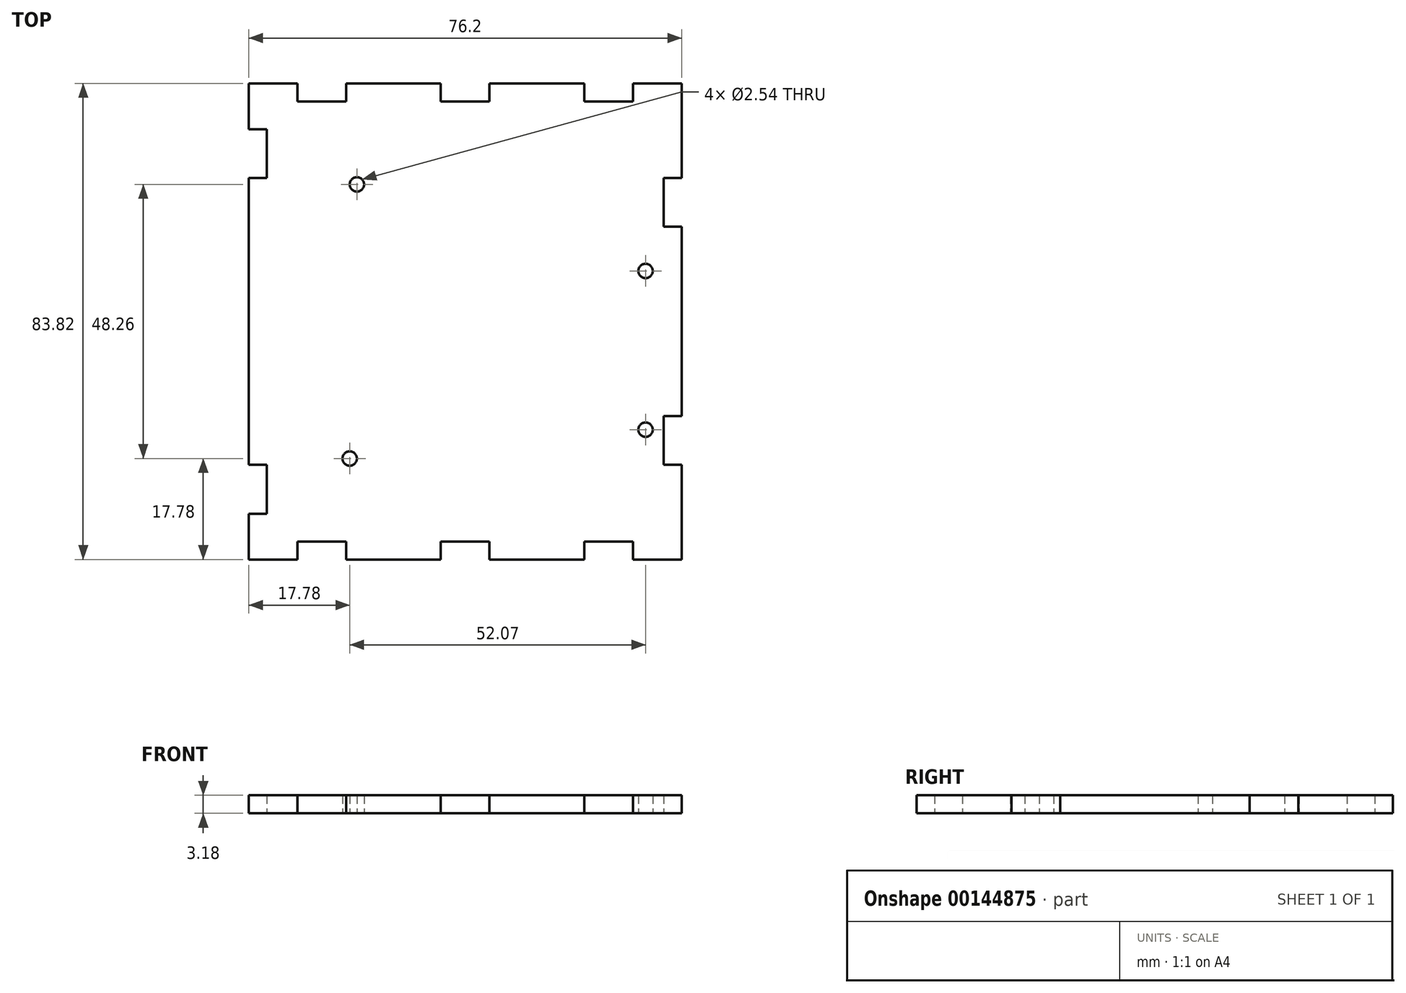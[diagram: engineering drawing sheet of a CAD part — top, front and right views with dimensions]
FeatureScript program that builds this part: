
annotation { "Feature Type Name" : "Feature", "Feature Type Description" : "" }
export const myFeature = defineFeature(function(context is Context, id is Id, definition is map)
    precondition{}
    {
        {
            var Q0;
            Q0=qCreatedBy(makeId("Top.planeOp"),FACE);
            var sketch = newSketch(context, id + "F0", { "sketchPlane" : qUnion([Q0])});
            skLineSegment(sketch, "E0.bottom", {"start": v(-38.1, 41.91) * mm, "end": v(38.1, 41.91) * mm});
            skLineSegment(sketch, "E0.top", {"start": v(-38.1, -41.91) * mm, "end": v(38.1, -41.91) * mm});
            skLineSegment(sketch, "E0.left", {"start": v(-38.1, 41.91) * mm, "end": v(-38.1, -41.9) * mm});
            skLineSegment(sketch, "E0.right", {"start": v(38.1, 41.91) * mm, "end": v(38.1, -41.9) * mm});
            skPoint(sketch, "E0.middle", {"position": v(0, 0) * mm});
            skCircle(sketch, "E1", {"center": v(-19.05, 24.13) * mm, "radius": 1.27 * mm});
            skCircle(sketch, "E2", {"center": v(-20.32, -24.13) * mm, "radius": 1.27 * mm});
            skCircle(sketch, "E3", {"center": v(31.75, 8.9) * mm, "radius": 1.27 * mm});
            skCircle(sketch, "E4", {"center": v(31.75, -19.05) * mm, "radius": 1.27 * mm});
            skPoint(sketch, "E5", {"position": v(-29.53, 41.91) * mm});
            skPoint(sketch, "E6", {"position": v(-20.95, 41.9) * mm});
            skPoint(sketch, "E7", {"position": v(0, 41.9) * mm});
            skPoint(sketch, "E8", {"position": v(0, 41.91) * mm});
            skPoint(sketch, "E9", {"position": v(20.94, 41.91) * mm});
            skPoint(sketch, "E10", {"position": v(29.51, 41.91) * mm});
            skLineSegment(sketch, "E11", {"start": v(-29.53, 41.91) * mm, "end": v(-29.53, 38.74) * mm});
            skLineSegment(sketch, "E12", {"start": v(-29.53, 38.74) * mm, "end": v(-20.95, 38.74) * mm});
            skLineSegment(sketch, "E13", {"start": v(-20.95, 38.74) * mm, "end": v(-20.95, 41.9) * mm});
            skLineSegment(sketch, "E14", {"start": v(0, 38.74) * mm, "end": v(0, 41.9) * mm});
            skLineSegment(sketch, "E15", {"start": v(20.94, 41.91) * mm, "end": v(20.94, 38.74) * mm});
            skLineSegment(sketch, "E16", {"start": v(20.94, 38.74) * mm, "end": v(29.51, 38.74) * mm});
            skLineSegment(sketch, "E17", {"start": v(29.51, 38.74) * mm, "end": v(29.51, 41.91) * mm});
            skLineSegment(sketch, "E18", {"start": v(0, 41.91) * mm, "end": v(-4.3, 41.91) * mm});
            skPoint(sketch, "E19", {"position": v(4.3, 41.91) * mm});
            skLineSegment(sketch, "E20", {"start": v(0, 41.91) * mm, "end": v(4.3, 41.91) * mm});
            skLineSegment(sketch, "E21", {"start": v(4.3, 41.91) * mm, "end": v(4.3, 38.74) * mm});
            skLineSegment(sketch, "E22", {"start": v(4.3, 38.74) * mm, "end": v(-4.3, 38.74) * mm});
            skLineSegment(sketch, "E23", {"start": v(-4.3, 38.74) * mm, "end": v(-4.3, 41.91) * mm});
            skPoint(sketch, "E24", {"position": v(-29.53, -41.9) * mm});
            skPoint(sketch, "E25", {"position": v(-20.95, -41.9) * mm});
            skPoint(sketch, "E26", {"position": v(-4.3, -41.91) * mm});
            skPoint(sketch, "E27", {"position": v(4.3, -41.91) * mm});
            skPoint(sketch, "E28", {"position": v(20.94, -41.91) * mm});
            skPoint(sketch, "E29", {"position": v(29.51, -41.91) * mm});
            skLineSegment(sketch, "E30.bottom", {"start": v(-29.53, -41.91) * mm, "end": v(-20.95, -41.91) * mm});
            skLineSegment(sketch, "E30.top", {"start": v(-29.53, -38.74) * mm, "end": v(-20.95, -38.74) * mm});
            skLineSegment(sketch, "E30.left", {"start": v(-29.53, -41.9) * mm, "end": v(-29.53, -38.74) * mm});
            skLineSegment(sketch, "E30.right", {"start": v(-20.95, -41.9) * mm, "end": v(-20.95, -38.74) * mm});
            skLineSegment(sketch, "E31.bottom", {"start": v(-4.3, -41.91) * mm, "end": v(4.3, -41.91) * mm});
            skLineSegment(sketch, "E31.top", {"start": v(-4.3, -38.74) * mm, "end": v(4.3, -38.74) * mm});
            skLineSegment(sketch, "E31.left", {"start": v(-4.3, -41.91) * mm, "end": v(-4.3, -38.74) * mm});
            skLineSegment(sketch, "E31.right", {"start": v(4.3, -41.91) * mm, "end": v(4.3, -38.74) * mm});
            skLineSegment(sketch, "E32.bottom", {"start": v(20.94, -41.91) * mm, "end": v(29.51, -41.91) * mm});
            skLineSegment(sketch, "E32.top", {"start": v(20.94, -38.74) * mm, "end": v(29.51, -38.74) * mm});
            skLineSegment(sketch, "E32.left", {"start": v(20.94, -41.91) * mm, "end": v(20.94, -38.74) * mm});
            skLineSegment(sketch, "E32.right", {"start": v(29.51, -41.91) * mm, "end": v(29.51, -38.74) * mm});
            skPoint(sketch, "E33", {"position": v(38.1, 20.96) * mm});
            skPoint(sketch, "E34", {"position": v(38.1, -20.96) * mm});
            skPoint(sketch, "E35", {"position": v(38.1, 0) * mm});
            skPoint(sketch, "E36", {"position": v(38.1, 25.25) * mm});
            skPoint(sketch, "E37", {"position": v(38.1, 16.66) * mm});
            skPoint(sketch, "E38", {"position": v(38.1, -16.66) * mm});
            skPoint(sketch, "E39", {"position": v(38.1, -25.25) * mm});
            skLineSegment(sketch, "E40.bottom", {"start": v(38.1, 25.25) * mm, "end": v(34.93, 25.25) * mm});
            skLineSegment(sketch, "E40.top", {"start": v(38.1, 16.66) * mm, "end": v(34.93, 16.66) * mm});
            skLineSegment(sketch, "E40.left", {"start": v(38.1, 25.25) * mm, "end": v(38.1, 16.66) * mm});
            skLineSegment(sketch, "E40.right", {"start": v(34.93, 25.25) * mm, "end": v(34.93, 16.66) * mm});
            skLineSegment(sketch, "E41.bottom", {"start": v(38.1, -16.66) * mm, "end": v(34.93, -16.66) * mm});
            skLineSegment(sketch, "E41.top", {"start": v(38.1, -25.25) * mm, "end": v(34.93, -25.25) * mm});
            skLineSegment(sketch, "E41.left", {"start": v(38.1, -16.66) * mm, "end": v(38.1, -25.25) * mm});
            skLineSegment(sketch, "E41.right", {"start": v(34.93, -16.66) * mm, "end": v(34.93, -25.25) * mm});
            skLineSegment(sketch, "E42.bottom", {"start": v(-38.1, 25.25) * mm, "end": v(-34.92, 25.25) * mm});
            skLineSegment(sketch, "E42.top", {"start": v(-38.1, 33.83) * mm, "end": v(-34.92, 33.83) * mm});
            skLineSegment(sketch, "E42.left", {"start": v(-38.1, 25.25) * mm, "end": v(-38.1, 33.83) * mm});
            skLineSegment(sketch, "E42.right", {"start": v(-34.92, 25.25) * mm, "end": v(-34.92, 33.83) * mm});
            skLineSegment(sketch, "E43.bottom", {"start": v(-38.1, -25.25) * mm, "end": v(-34.93, -25.25) * mm});
            skLineSegment(sketch, "E43.top", {"start": v(-38.1, -33.83) * mm, "end": v(-34.93, -33.83) * mm});
            skLineSegment(sketch, "E43.left", {"start": v(-38.1, -25.25) * mm, "end": v(-38.1, -33.83) * mm});
            skLineSegment(sketch, "E43.right", {"start": v(-34.93, -25.25) * mm, "end": v(-34.93, -33.83) * mm});
            skSolve(sketch);
        }
        {
            var Q0;
            Q0=makeQuery(id+"F0.imprint","IMPRINT",FACE,{"disambiguationData":[TD([[makeQuery(id+"F0.imprint","IMPRINT",EDGE,{"derivedFrom":sQuery(id+"F0.wireOp",EDGE,"E0.bottom")}),-1.0]])]});
            extrude(context, id + "F1", {"entities" : qUnion([Q0]), "depth" : 3.17 * mm});
        }
    });
